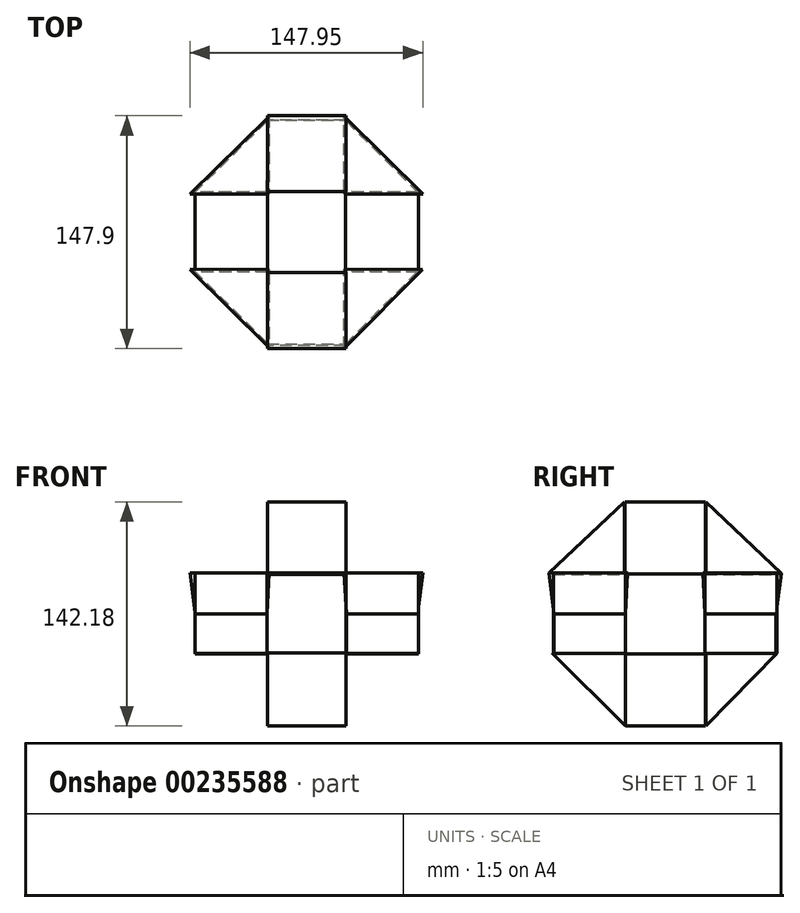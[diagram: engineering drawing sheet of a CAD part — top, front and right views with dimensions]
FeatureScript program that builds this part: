
annotation { "Feature Type Name" : "Feature", "Feature Type Description" : "" }
export const myFeature = defineFeature(function(context is Context, id is Id, definition is map)
    precondition{}
    {
        {
            var Q0;
            Q0=qCreatedBy(makeId("Front.planeOp"),FACE);
            var sketch = newSketch(context, id + "F0", { "sketchPlane" : qUnion([Q0])});
            skLineSegment(sketch, "E0.bottom", {"start": v(-25.04, -25.01) * mm, "end": v(25.04, -25.01) * mm});
            skLineSegment(sketch, "E0.top", {"start": v(-25.04, 25.01) * mm, "end": v(25.04, 25.01) * mm});
            skLineSegment(sketch, "E0.left", {"start": v(-25.04, -25.01) * mm, "end": v(-25.04, 25.01) * mm});
            skLineSegment(sketch, "E0.right", {"start": v(25.04, -25.01) * mm, "end": v(25.04, 25.01) * mm});
            skPoint(sketch, "E0.middle", {"position": v(0, 0) * mm});
            skSolve(sketch);
        }
        {
            var Q0;
            Q0=qCreatedBy(makeId("Right.planeOp"),FACE);
            var sketch = newSketch(context, id + "F1", { "sketchPlane" : qUnion([Q0])});
            skLineSegment(sketch, "E1.bottom", {"start": v(-25.38, -25.38) * mm, "end": v(25.38, -25.38) * mm});
            skLineSegment(sketch, "E1.top", {"start": v(-25.38, 25.38) * mm, "end": v(25.38, 25.38) * mm});
            skLineSegment(sketch, "E1.left", {"start": v(-25.38, -25.38) * mm, "end": v(-25.38, 25.38) * mm});
            skLineSegment(sketch, "E1.right", {"start": v(25.38, -25.38) * mm, "end": v(25.38, 25.38) * mm});
            skPoint(sketch, "E1.middle", {"position": v(0, 0) * mm});
            skPoint(sketch, "E2.endSnap0", {"position": v(0, 25.38) * mm});
            skSolve(sketch);
        }
        {
            var Q0;
            Q0=makeQuery(id+"F0.imprint","IMPRINT",FACE,{"disambiguationData":[TD([[makeQuery(id+"F0.imprint","IMPRINT",EDGE,{"derivedFrom":sQuery(id+"F0.wireOp",EDGE,"E0.bottom")}),1.0]])]});
            extrude(context, id + "F2", {"entities" : qUnion([Q0]), "depth" : 71 * mm, "hasSecondDirection" : true, "secondDirectionOppositeDirection" : true, "secondDirectionDepth" : 71 * mm});
        }
        {
            var Q0;
            Q0 = qSketchRegion(id + "F1", true);
            extrude(context, id + "F3", {"entities" : qUnion([Q0]), "operationType" : NewBodyOperationType.ADD, "depth" : 71 * mm, "hasSecondDirection" : true, "secondDirectionOppositeDirection" : true, "secondDirectionDepth" : 71 * mm});
        }
        {
            var Q0;
            Q0=qCreatedBy(makeId("Top.planeOp"),FACE);
            var sketch = newSketch(context, id + "F4", { "sketchPlane" : qUnion([Q0])});
            skLineSegment(sketch, "E3.bottom", {"start": v(-24.72, 25.6) * mm, "end": v(24.72, 25.6) * mm});
            skLineSegment(sketch, "E3.top", {"start": v(-24.72, -25.6) * mm, "end": v(24.72, -25.6) * mm});
            skLineSegment(sketch, "E3.left", {"start": v(-24.72, 25.6) * mm, "end": v(-24.72, -25.6) * mm});
            skLineSegment(sketch, "E3.right", {"start": v(24.72, 25.6) * mm, "end": v(24.72, -25.6) * mm});
            skPoint(sketch, "E3.middle", {"position": v(0, 0) * mm});
            skSolve(sketch);
        }
        {
            var Q0;
            Q0 = qSketchRegion(id + "F4", true);
            extrude(context, id + "F5", {"entities" : qUnion([Q0]), "operationType" : NewBodyOperationType.ADD, "depth" : 71 * mm, "hasSecondDirection" : true, "secondDirectionOppositeDirection" : true, "secondDirectionDepth" : 71 * mm});
        }
        {
            var Q0;
            Q0=qCreatedBy(makeId("Top.planeOp"),FACE);
            var sketch = newSketch(context, id + "F6", { "sketchPlane" : qUnion([Q0])});
            skLineSegment(sketch, "E4", {"start": v(-25.16, 70.44) * mm, "end": v(-70.88, 25.38) * mm});
            skLineSegment(sketch, "E5", {"start": v(-70.88, 25.38) * mm, "end": v(-25.38, 25.38) * mm});
            skLineSegment(sketch, "E6", {"start": v(-25.38, 25.38) * mm, "end": v(-25.16, 70.44) * mm});
            skLineSegment(sketch, "E7", {"start": v(25.16, 70.44) * mm, "end": v(70.44, 25.38) * mm});
            skLineSegment(sketch, "E8", {"start": v(70.44, 25.38) * mm, "end": v(24.94, 25.6) * mm});
            skLineSegment(sketch, "E9", {"start": v(24.94, 25.6) * mm, "end": v(25.16, 70.44) * mm});
            skLineSegment(sketch, "E10", {"start": v(70.44, 25.38) * mm, "end": v(70.44, -25.16) * mm});
            skLineSegment(sketch, "E11", {"start": v(70.44, -25.16) * mm, "end": v(25.16, -24.94) * mm});
            skLineSegment(sketch, "E12", {"start": v(25.16, -24.94) * mm, "end": v(25.16, -70.66) * mm});
            skLineSegment(sketch, "E13", {"start": v(25.16, -70.66) * mm, "end": v(70.44, -25.16) * mm});
            skLineSegment(sketch, "E14", {"start": v(25.16, -70.66) * mm, "end": v(-25.16, -70.42) * mm});
            skLineSegment(sketch, "E15", {"start": v(-25.16, -70.42) * mm, "end": v(-25.16, -24.94) * mm});
            skLineSegment(sketch, "E16", {"start": v(-25.16, -24.94) * mm, "end": v(-70.88, -25.16) * mm});
            skLineSegment(sketch, "E17", {"start": v(-70.88, -25.16) * mm, "end": v(-25.16, -70.42) * mm});
            skLineSegment(sketch, "E18", {"start": v(-70.88, -25.16) * mm, "end": v(-70.88, 25.38) * mm});
            skSolve(sketch);
        }
        {
            var Q0;
            Q0 = qSketchRegion(id + "F6", true);
            extrude(context, id + "F7", {"entities" : qUnion([Q0]), "depth" : 26 * mm, "hasDraft" : true, "draftAngle" : 3 * degree, "hasSecondDirection" : true, "secondDirectionOppositeDirection" : true, "secondDirectionDepth" : 25 * mm});
        }
        {
            var Q0;
            Q0=qCreatedBy(makeId("Right.planeOp"),FACE);
            var sketch = newSketch(context, id + "F8", { "sketchPlane" : qUnion([Q0])});
            skLineSegment(sketch, "E19", {"start": v(-25.81, 71.1) * mm, "end": v(-73.94, 26.03) * mm});
            skLineSegment(sketch, "E20", {"start": v(-73.94, 26.03) * mm, "end": v(-25.81, 26.03) * mm});
            skLineSegment(sketch, "E21", {"start": v(-25.81, 26.03) * mm, "end": v(-25.81, 71.1) * mm});
            skLineSegment(sketch, "E22", {"start": v(25.81, 71.1) * mm, "end": v(25.81, 25.81) * mm});
            skLineSegment(sketch, "E23", {"start": v(25.81, 25.81) * mm, "end": v(73.94, 25.81) * mm});
            skLineSegment(sketch, "E24", {"start": v(73.94, 25.81) * mm, "end": v(25.81, 71.1) * mm});
            skLineSegment(sketch, "E25", {"start": v(73.94, 25.81) * mm, "end": v(71.1, -25.16) * mm});
            skLineSegment(sketch, "E26", {"start": v(71.1, -25.16) * mm, "end": v(25.81, -71.1) * mm});
            skLineSegment(sketch, "E27", {"start": v(25.81, -71.1) * mm, "end": v(25.81, -25.16) * mm});
            skLineSegment(sketch, "E28", {"start": v(25.81, -25.16) * mm, "end": v(71.1, -25.16) * mm});
            skLineSegment(sketch, "E29", {"start": v(25.81, -71.1) * mm, "end": v(-25.38, -71.1) * mm});
            skLineSegment(sketch, "E30", {"start": v(-25.38, -71.1) * mm, "end": v(-25.38, -24.72) * mm});
            skLineSegment(sketch, "E31", {"start": v(-25.38, -24.72) * mm, "end": v(-71.97, -24.72) * mm});
            skLineSegment(sketch, "E32", {"start": v(-71.97, -24.72) * mm, "end": v(-25.38, -71.1) * mm});
            skSolve(sketch);
        }
        {
            var Q0;
            Q0 = qSketchRegion(id + "F8", true);
            extrude(context, id + "F9", {"entities" : qUnion([Q0]), "depth" : 25 * mm, "hasSecondDirection" : true, "secondDirectionOppositeDirection" : true, "secondDirectionDepth" : 25 * mm});
        }
    });
